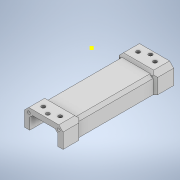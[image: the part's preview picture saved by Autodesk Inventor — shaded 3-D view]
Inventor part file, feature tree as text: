
AUTODESK INVENTOR PART (.ipt)
format: ipt  version: 2022 (Build 260153000, 153)  size: 687,104 bytes
history: native  units: in
note: dims shown in document units (in); Inventor stores cm internally (conversion verified against a paired STEP export)
features: sketch x29, extrude x27, projected_geometry x18, chamfer x7
ambient origin geometry x8: Origin, YZ Plane, XZ Plane, XY Plane, X Axis, Y Axis, Z Axis, Center Point
bodies: Solid1 (feature_tree)
feature tree (81):
  extrude  "Extrusion1"  TaperAngle=75.0deg  [1 undecoded]
  extrude  "Extrusion2"  Depth=0.0787in TaperAngle=0.0deg
  chamfer  "Chamfer1"  Distance=0.1181in
  chamfer  "Chamfer2"  Distance=0.1969in Angle=45.0deg
  chamfer  "Chamfer3"  Distance=0.1181in Angle=45.0deg
  extrude  "Extrusion3"  Depth=0.0787in
  extrude  "Extrusion4"  Depth=0.0787in
  extrude  "Extrusion5"  Depth=0.1969in TaperAngle=0.0deg
  extrude  "Extrusion6"  Depth=0.5906in TaperAngle=0.0deg
  extrude  "Extrusion7"  Depth=2.7559in
  chamfer  "Chamfer4"  Distance=0.2756in
  extrude  "Extrusion8"  Depth=0.3937in
  extrude  "Extrusion16"  Depth=0.3937in
  extrude  "Extrusion17"  Depth=0.3937in TaperAngle=0.0deg
  extrude  "Extrusion18"  Depth=0.0787in TaperAngle=45.0deg
  extrude  "Extrusion19"  Depth=0.3937in
  chamfer  "Chamfer7"  Distance=1.1417in
  chamfer  "Chamfer8"  Distance=0.1575in
  extrude  "Extrusion20"  Depth=0.3937in
  extrude  "Extrusion21"  Depth=0.3937in TaperAngle=0.0deg
  extrude  "Extrusion22"  Depth=0.3937in
  sketch  "Sketch25"  dims[d40=0.7874in]
  extrude  "Extrusion23"  Depth=0.3937in
  extrude  "Extrusion24"  Depth=0.1181in TaperAngle=0.0deg
  sketch  "Sketch28"  dims[d42=0.894in]
  extrude  "Extrusion27"  Depth=0.3937in TaperAngle=0.0deg
  extrude  "Extrusion28"  Depth=0.5906in
  extrude  "Extrusion29"  Depth=0.5906in
  extrude  "Extrusion30"  Depth=0.5906in
  extrude  "Extrusion31"  Depth=0.5906in
  chamfer  "Chamfer9"  Distance=1.1811in
  extrude  "Extrusion32"  Depth=0.1181in
  extrude  "Extrusion33"  Depth=0.3937in TaperAngle=0.0deg
  extrude  "Extrusion34"  Depth=0.3937in TaperAngle=0.0deg
  extrude  "Extrusion35"  Depth=0.1181in TaperAngle=45.0deg
  extrude  "Extrusion36"  Depth=0.1181in TaperAngle=45.0deg
  sketch  "Sketch1"  dims[d0=3.1496in d4=75.0deg]
  sketch  "Sketch2"  dims[d5=0.1575in d6=2.7559in d7=0.0in d8=0.1181in d9=0.0in d10=0.1969in d11=0.0787in d12=45.0deg d13=0.1181in d14=0.0787in d15=45.0deg]
  projected_geometry  "Projected Loop1"
  sketch  "Sketch3"  dims[d16=0.1181in d17=0.0787in d18=45.0deg d19=0.0787in]
  sketch  "Sketch4"  dims[d20=0.0787in d22=0.0787in]
  sketch  "Sketch5"  dims[d23=0.0787in d24=0.1969in d25=0.0in]
  sketch  "Sketch7"  dims[d26=0.0787in d27=0.5906in d28=0.0in]
  sketch  "Sketch8"  dims[d29=1.5748in d30=2.7559in]
  sketch  "Sketch9"  dims[d31=0.7874in]
  sketch  "Sketch17"  dims[d32=0.8858in]
  projected_geometry  "Projected Loop4"
  sketch  "Sketch18"  dims[d33=1.5748in]
  sketch  "Sketch19"  dims[d34=1.7717in]
  sketch  "Sketch20"  dims[d35=1.1811in]
  projected_geometry  "Projected Loop5"
  sketch  "Sketch21"  dims[d36=0.7874in]
  projected_geometry  "Projected Loop6"
  sketch  "Sketch22"  dims[d37=0.0787in]
  projected_geometry  "Projected Loop7"
  sketch  "Sketch23"  dims[d38=0.7874in]
  projected_geometry  "Projected Loop8"
  projected_geometry  "Projected Loop9"
  projected_geometry  "Projected Loop10"
  projected_geometry  "Projected Loop11"
  projected_geometry  "Projected Loop12"
  sketch  "Sketch24"  dims[d39=0.0787in]
  projected_geometry  "Projected Loop13"
  sketch  "Sketch26"  dims[d41=0.9115in]
  projected_geometry  "Projected Loop14"
  sketch  "Sketch37"  dims[d43=0.1181in]
  projected_geometry  "Projected Loop18"
  sketch  "Sketch38"  dims[d44=0.1181in]
  projected_geometry  "Projected Loop19"
  sketch  "Sketch40"  dims[d45=1.5748in]
  projected_geometry  "Projected Loop20"
  sketch  "Sketch42"  dims[d46=0.0in]
  projected_geometry  "Projected Loop21"
  sketch  "Sketch43"  dims[d47=1.0787in]
  projected_geometry  "Projected Loop22"
  sketch  "Sketch46"  dims[d48=1.3386in]
  sketch  "Sketch48"  dims[d49=0.5197in]
  sketch  "Sketch49"  dims[d50=1.0787in]
  sketch  "Sketch50"  dims[d51=0.0in]
  sketch  "Sketch51"  dims[d52=0.0787in d53=0.2756in d54=0.2657in d55=0.5315in d56=0.3543in d57=0.0in d58=0.0394in d59=0.0787in d60=45.0deg d61=0.5709in d62=1.1417in d63=0.1575in d64=0.1575in d65=39.3307in d66=0.0in d106=1.378in d107=1.378in d108=0.1181in d109=0.0in d110=2.874in d111=0.0in d112=0.5906in d113=0.5906in d114=0.5906in d115=0.5906in d116=1.1811in d117=0.1181in d118=2.874in d119=0.0in d120=2.874in d121=0.0in d122=0.1181in d123=0.0787in d124=45.0deg d125=0.1181in d126=0.0787in d127=45.0deg d128=0.7421in d129=0.1181in d130=0.0in d131=0.0787in d132=0.0787in d133=0.0787in d134=0.0787in d135=7.874in d136=0.0in d137=0.3937in d138=0.0in d139=0.8169in d140=0.0in d141=0.8169in d142=0.0in d147=0.0098in d148=0.0in d149=0.0098in d150=0.0in d151=0.0098in d152=0.0in d153=0.0984in d154=0.7874in d155=0.0in d156=0.0984in d157=0.7874in d158=0.0in d159=0.1181in d160=0.0787in d161=45.0deg d162=0.1181in d163=1.5748in d165=360.0deg d167=0.5906in d168=0.0in d170=1.5748in d171=0.1181in d172=360.0deg d173=0.5906in d174=0.0in d175=0.3543in d176=0.1575in d177=0.1575in d178=1.378in d179=0.0in d180=0.0in d181=0.0in d182=0.3937in d183=0.0in]
  projected_geometry  "Projected Loop23"
note: 1 required parameter value undecoded (feature->parameter linkage not recoverable at this tier; creation-order binding heuristic only, values carry confidence <= 0.55)
